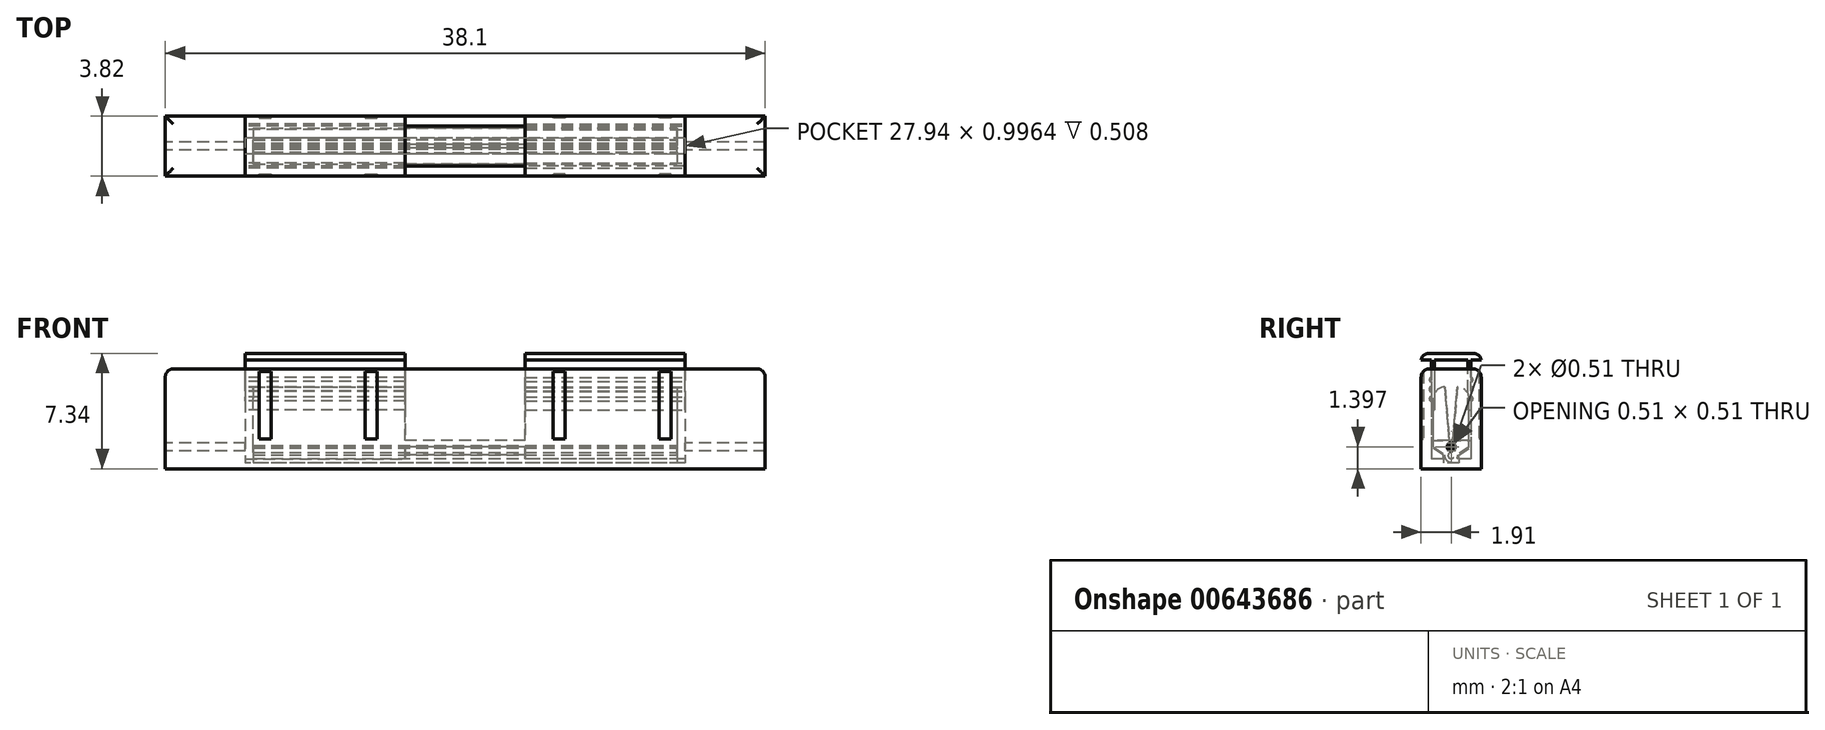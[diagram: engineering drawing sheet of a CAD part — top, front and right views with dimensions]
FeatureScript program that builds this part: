
annotation { "Feature Type Name" : "Feature", "Feature Type Description" : "" }
export const myFeature = defineFeature(function(context is Context, id is Id, definition is map)
    precondition{}
    {
        {
            var Q0;
            Q0=qCreatedBy(makeId("Top.planeOp"),FACE);
            var sketch = newSketch(context, id + "F0", { "sketchPlane" : qUnion([Q0])});
            skLineSegment(sketch, "E0.bottom", {"start": v(19.05, -1.9) * mm, "end": v(-19.05, -1.9) * mm});
            skLineSegment(sketch, "E0.top", {"start": v(19.05, 1.9) * mm, "end": v(-19.05, 1.9) * mm});
            skLineSegment(sketch, "E0.left", {"start": v(19.05, -1.9) * mm, "end": v(19.05, 1.9) * mm});
            skLineSegment(sketch, "E0.right", {"start": v(-19.05, -1.9) * mm, "end": v(-19.05, 1.9) * mm});
            skPoint(sketch, "E0.middle", {"position": v(0, 0) * mm});
            skLineSegment(sketch, "E1", {"start": v(0, 6.77) * mm, "end": v(0, -8.48) * mm, "construction": true});
            skLineSegment(sketch, "E2.bottom", {"start": v(-13.97, 1.27) * mm, "end": v(-3.81, 1.27) * mm});
            skLineSegment(sketch, "E2.top", {"start": v(-13.97, -1.27) * mm, "end": v(-3.81, -1.27) * mm});
            skLineSegment(sketch, "E2.left", {"start": v(-13.97, 1.27) * mm, "end": v(-13.97, -1.27) * mm});
            skLineSegment(sketch, "E2.right", {"start": v(-3.81, 1.27) * mm, "end": v(-3.81, -1.27) * mm});
            skLineSegment(sketch, "E3.MirrorCS", {"start": v(3.81, 1.27) * mm, "end": v(3.81, -1.27) * mm});
            skLineSegment(sketch, "E4.MirrorCS", {"start": v(13.97, 1.27) * mm, "end": v(3.81, 1.27) * mm});
            skLineSegment(sketch, "E5.MirrorCS", {"start": v(13.97, -1.27) * mm, "end": v(3.81, -1.27) * mm});
            skLineSegment(sketch, "E6.MirrorCS", {"start": v(13.97, 1.27) * mm, "end": v(13.97, -1.27) * mm});
            skLineSegment(sketch, "E7", {"start": v(13.08, 1.9) * mm, "end": v(13.08, 1.78) * mm});
            skLineSegment(sketch, "E8", {"start": v(13.08, 1.78) * mm, "end": v(12.32, 1.78) * mm});
            skLineSegment(sketch, "E9", {"start": v(12.32, 1.78) * mm, "end": v(12.32, 1.9) * mm});
            skLineSegment(sketch, "E10", {"start": v(26.93, 0) * mm, "end": v(-31.8, 0) * mm, "construction": true});
            skPoint(sketch, "E10.startSnap0", {"position": v(19.05, 0) * mm});
            skLineSegment(sketch, "E11", {"start": v(6.35, 1.9) * mm, "end": v(6.35, 1.78) * mm});
            skLineSegment(sketch, "E12", {"start": v(6.35, 1.78) * mm, "end": v(5.59, 1.78) * mm});
            skLineSegment(sketch, "E13", {"start": v(5.59, 1.78) * mm, "end": v(5.59, 1.9) * mm});
            skLineSegment(sketch, "E14.MirrorCS", {"start": v(6.35, -1.9) * mm, "end": v(6.35, -1.78) * mm});
            skLineSegment(sketch, "E15.MirrorCS", {"start": v(6.35, -1.78) * mm, "end": v(5.59, -1.78) * mm});
            skLineSegment(sketch, "E16.MirrorCS", {"start": v(5.59, -1.78) * mm, "end": v(5.59, -1.9) * mm});
            skLineSegment(sketch, "E17.MirrorCS", {"start": v(12.32, -1.78) * mm, "end": v(12.32, -1.9) * mm});
            skLineSegment(sketch, "E18.MirrorCS", {"start": v(13.08, -1.78) * mm, "end": v(12.32, -1.78) * mm});
            skLineSegment(sketch, "E19.MirrorCS", {"start": v(13.08, -1.9) * mm, "end": v(13.08, -1.78) * mm});
            skLineSegment(sketch, "E20.MirrorCS", {"start": v(-6.35, 1.78) * mm, "end": v(-5.59, 1.78) * mm});
            skLineSegment(sketch, "E21.MirrorCS", {"start": v(-5.59, 1.78) * mm, "end": v(-5.59, 1.9) * mm});
            skLineSegment(sketch, "E22.MirrorCS", {"start": v(-6.35, 1.9) * mm, "end": v(-6.35, 1.78) * mm});
            skLineSegment(sketch, "E23.MirrorCS", {"start": v(-12.32, 1.78) * mm, "end": v(-12.32, 1.9) * mm});
            skLineSegment(sketch, "E24.MirrorCS", {"start": v(-13.08, 1.78) * mm, "end": v(-12.32, 1.78) * mm});
            skLineSegment(sketch, "E25.MirrorCS", {"start": v(-13.08, 1.9) * mm, "end": v(-13.08, 1.78) * mm});
            skLineSegment(sketch, "E26.MirrorCS", {"start": v(-6.35, -1.9) * mm, "end": v(-6.35, -1.78) * mm});
            skLineSegment(sketch, "E27.MirrorCS", {"start": v(-6.35, -1.78) * mm, "end": v(-5.59, -1.78) * mm});
            skLineSegment(sketch, "E28.MirrorCS", {"start": v(-5.59, -1.78) * mm, "end": v(-5.59, -1.9) * mm});
            skLineSegment(sketch, "E29.MirrorCS", {"start": v(-13.08, -1.9) * mm, "end": v(-13.08, -1.78) * mm});
            skLineSegment(sketch, "E30.MirrorCS", {"start": v(-13.08, -1.78) * mm, "end": v(-12.32, -1.78) * mm});
            skLineSegment(sketch, "E31.MirrorCS", {"start": v(-12.32, -1.78) * mm, "end": v(-12.32, -1.9) * mm});
            skSolve(sketch);
        }
        {
            var Q0;
            Q0=makeQuery(id+"F0.imprint","IMPRINT",FACE,{"disambiguationData":[TD([[makeQuery(id+"F0.imprint","IMPRINT",EDGE,{"derivedFrom":sQuery(id+"F0.wireOp",EDGE,"E0.top")}),1.0]])]});
            extrude(context, id + "F1", {"entities" : qUnion([Q0]), "depth" : 6.35 * mm, "offsetDistance" : 25.4 * mm});
        }
        {
            var Q0;
            Q0=makeQuery(id+"F0.imprint","IMPRINT",FACE,{"disambiguationData":[TD([[makeQuery(id+"F0.imprint","IMPRINT",EDGE,{"derivedFrom":sQuery(id+"F0.wireOp",EDGE,"E2.bottom")}),-1.0]])]});
            var Q1;
            Q1=makeQuery(id+"F0.imprint","IMPRINT",FACE,{"disambiguationData":[TD([[makeQuery(id+"F0.imprint","IMPRINT",EDGE,{"derivedFrom":sQuery(id+"F0.wireOp",EDGE,"E3.MirrorCS")}),1.0]])]});
            extrude(context, id + "F2", {"entities" : qUnion([Q0, Q1]), "operationType" : NewBodyOperationType.ADD, "depth" : 0.64 * mm, "offsetDistance" : 25.4 * mm});
        }
        {
            var Q0;
            Q0=makeQuery(id+"F1.opExtrude","SWEPT_FACE",FACE,{"disambiguationData":[OSD([sQuery(id+"F0.wireOp",EDGE,"E2.left")])]});
            var sketch = newSketch(context, id + "F3", { "sketchPlane" : qUnion([Q0])});
            skLineSegment(sketch, "E32.bottom", {"start": v(0.5, 0.38) * mm, "end": v(-0.5, 0.38) * mm});
            skLineSegment(sketch, "E32.top", {"start": v(1.27, 5.46) * mm, "end": v(-1.27, 5.46) * mm});
            skLineSegment(sketch, "E32.left", {"start": v(1.27, 1.4) * mm, "end": v(1.27, 5.46) * mm});
            skLineSegment(sketch, "E32.right", {"start": v(-1.27, 1.4) * mm, "end": v(-1.27, 5.46) * mm});
            skLineSegment(sketch, "E33", {"start": v(0, 0) * mm, "end": v(0, 8.58) * mm, "construction": true});
            skPoint(sketch, "E34", {"position": v(0, 0.99) * mm});
            skLineSegment(sketch, "E35", {"start": v(0.5, 0.89) * mm, "end": v(0.5, 0.38) * mm});
            skLineSegment(sketch, "E36.MirrorCS", {"start": v(-0.5, 0.89) * mm, "end": v(-0.5, 0.38) * mm});
            skPoint(sketch, "E37.orphan", {"position": v(-0.5, 0.38) * mm});
            skPoint(sketch, "E38.orphan", {"position": v(1.27, 0.38) * mm});
            skLineSegment(sketch, "E39", {"start": v(1.27, 1.4) * mm, "end": v(0.5, 0.89) * mm});
            skLineSegment(sketch, "E40.MirrorCS", {"start": v(-1.27, 1.4) * mm, "end": v(-0.5, 0.89) * mm});
            skSolve(sketch);
        }
        {
            var Q0;
            Q0 = qSketchRegion(id + "F3", true);
            var Q1;
            Q1=makeQuery(id+"F1.opExtrude","SWEPT_FACE",FACE,{"disambiguationData":[OSD([sQuery(id+"F0.wireOp",EDGE,"E6.MirrorCS")])]});
            extrude(context, id + "F4", {"entities" : qUnion([Q0]), "operationType" : NewBodyOperationType.REMOVE, "endBound" : BoundingType.UP_TO_SURFACE, "depth" : 10.4 * mm, "endBoundEntityFace" : qUnion([Q1]), "offsetDistance" : 25.4 * mm});
        }
        {
            var Q0;
            Q0=qCreatedBy(makeId("Right.planeOp"),FACE);
            var sketch = newSketch(context, id + "F5", { "sketchPlane" : qUnion([Q0])});
            skCircle(sketch, "E41", {"center": v(0, 1.4) * mm, "radius": 0.1 * mm});
            skLineSegment(sketch, "E42.bottom", {"start": v(1.02, 5.08) * mm, "end": v(-1.02, 5.08) * mm});
            skLineSegment(sketch, "E42.top", {"start": v(1.02, 0) * mm, "end": v(-1.02, 0) * mm});
            skLineSegment(sketch, "E42.left", {"start": v(1.02, 5.08) * mm, "end": v(1.02, 0) * mm});
            skLineSegment(sketch, "E42.right", {"start": v(-1.02, 5.08) * mm, "end": v(-1.02, 0) * mm});
            skLineSegment(sketch, "E43", {"start": v(0, -1.4) * mm, "end": v(0, 7.34) * mm, "construction": true});
            skSolve(sketch);
        }
        {
            var Q0;
            Q0=makeQuery(id+"F1.opExtrude","SWEPT_FACE",FACE,{"disambiguationData":[OSD([sQuery(id+"F0.wireOp",EDGE,"E0.right")])]});
            var sketch = newSketch(context, id + "F6", { "sketchPlane" : qUnion([Q0])});
            skCircle(sketch, "E44", {"center": v(0, 1.4) * mm, "radius": 0.25 * mm});
            skSolve(sketch);
        }
        {
            var Q0;
            Q0 = qSketchRegion(id + "F6", true);
            extrude(context, id + "F7", {"entities" : qUnion([Q0]), "operationType" : NewBodyOperationType.REMOVE, "endBound" : BoundingType.THROUGH_ALL, "oppositeDirection" : true, "depth" : 25.4 * mm, "offsetDistance" : 25.4 * mm});
        }
        {
            var Q0;
            Q0=makeQuery(id+"F1.opExtrude","CAP_EDGE",EDGE,{"disambiguationData":[OSD([sQuery(id+"F0.wireOp",EDGE,"E0.right")])],"isStart":false});
            var Q1;
            Q1=makeQuery(id+"F1.opExtrude","CAP_EDGE",EDGE,{"disambiguationData":[OSD([sQuery(id+"F0.wireOp",EDGE,"E0.top")])],"isStart":false});
            var Q2;
            Q2=makeQuery(id+"F1.opExtrude","CAP_EDGE",EDGE,{"disambiguationData":[OSD([sQuery(id+"F0.wireOp",EDGE,"E0.bottom")])],"isStart":false});
            var Q3;
            Q3=makeQuery(id+"F1.opExtrude","CAP_EDGE",EDGE,{"disambiguationData":[OSD([sQuery(id+"F0.wireOp",EDGE,"E0.left")])],"isStart":false});
            fillet(context, id + "F8", {"entities" : qUnion([Q0, Q1, Q2, Q3]), "radius" : 0.5 * mm, "tangentPropagation" : true, "allowEdgeOverflow" : false});
        }
        {
            var Q0;
            Q0=makeQuery(id+"F1.opExtrude","SWEPT_FACE",FACE,{"disambiguationData":[OSD([sQuery(id+"F0.wireOp",EDGE,"E2.right")])]});
            var sketch = newSketch(context, id + "F9", { "sketchPlane" : qUnion([Q0])});
            skLineSegment(sketch, "E45.bottom", {"start": v(-0.38, 5.2) * mm, "end": v(0.38, 5.2) * mm});
            skLineSegment(sketch, "E45.top", {"start": v(-1.14, 0.38) * mm, "end": v(1.14, 0.38) * mm});
            skLineSegment(sketch, "E45.left", {"start": v(-1.14, 4.45) * mm, "end": v(-1.14, 0.38) * mm});
            skLineSegment(sketch, "E45.right", {"start": v(1.14, 4.45) * mm, "end": v(1.14, 0.38) * mm});
            skPoint(sketch, "E46.visualSharp", {"position": v(1.14, 5.2) * mm});
            skArc(sketch, "E46.filletArc", {"start": v(1.14, 4.45) * mm, "mid": v(0.92, 4.98) * mm, "end": v(0.38, 5.2) * mm});
            skPoint(sketch, "E47.visualSharp", {"position": v(-1.14, 5.2) * mm});
            skArc(sketch, "E47.filletArc", {"start": v(-0.38, 5.2) * mm, "mid": v(-0.92, 4.98) * mm, "end": v(-1.14, 4.45) * mm});
            skPoint(sketch, "E48.trimOffspring.end.orphan", {"position": v(0, 0.38) * mm});
            skLineSegment(sketch, "E49", {"start": v(-0.38, 5.2) * mm, "end": v(-0.09, 1.48) * mm});
            skLineSegment(sketch, "E50.MirrorCS", {"start": v(0.38, 5.2) * mm, "end": v(0.09, 1.48) * mm});
            skArc(sketch, "E51", {"start": v(-0.05, 1.03) * mm, "mid": v(0, 0.65) * mm, "end": v(0.05, 1.03) * mm});
            skLineSegment(sketch, "E52.trimOffspring", {"start": v(-0.08, 1.34) * mm, "end": v(-0.05, 1.03) * mm});
            skLineSegment(sketch, "E53.trimOffspring", {"start": v(0.08, 1.34) * mm, "end": v(0.05, 1.03) * mm});
            skArc(sketch, "E54", {"start": v(-0.42, 0.9) * mm, "mid": v(0, 0.42) * mm, "end": v(0.42, 0.9) * mm});
            skLineSegment(sketch, "E55", {"start": v(-0.42, 0.9) * mm, "end": v(-1.14, 1.4) * mm});
            skLineSegment(sketch, "E56.MirrorCS", {"start": v(0.42, 0.9) * mm, "end": v(1.14, 1.4) * mm});
            skArc(sketch, "E57", {"start": v(-0.09, 1.48) * mm, "mid": v(-0.2, 1.4) * mm, "end": v(-0.08, 1.34) * mm});
            skPoint(sketch, "E57.first.point", {"position": v(-0.08, 1.34) * mm});
            skPoint(sketch, "E57.second.point", {"position": v(-0.09, 1.48) * mm});
            skPoint(sketch, "E57.third.point", {"position": v(-0.2, 1.42) * mm});
            skArc(sketch, "E58.MirrorCS", {"start": v(0.08, 1.34) * mm, "mid": v(0.13, 1.4) * mm, "end": v(0.09, 1.48) * mm});
            skPoint(sketch, "E59.MirrorC.end.orphan", {"position": v(0.09, 1.48) * mm});
            skPoint(sketch, "E59.MirrorC.start.orphan", {"position": v(0.08, 1.34) * mm});
            skLineSegment(sketch, "E60.trimOffspring", {"start": v(0.08, 1.34) * mm, "end": v(0.08, 1.34) * mm});
            skLineSegment(sketch, "E61.trimOffspring", {"start": v(-0.08, 1.34) * mm, "end": v(-0.08, 1.34) * mm});
            skSolve(sketch);
        }
        {
            var Q0;
            {var subQ3=sQuery(id+"F9.wireOp",EDGE,"E46.filletArc");Q0=makeQuery(id+"F9.imprint","IMPRINT",FACE,{"disambiguationData":[TD([[makeQuery(id+"F9.imprint","IMPRINT",EDGE,{"derivedFrom":subQ3}),1.0]])]});}
            var Q1;
            Q1=makeQuery(id+"F4.boolean.opBoolean","MERGE",FACE,{"derivedFrom":[makeQuery(id+"F1.opExtrude","SWEPT_FACE",FACE,{"disambiguationData":[OSD([sQuery(id+"F0.wireOp",EDGE,"E2.left")])]}),makeQuery(id+"F4.opExtrude","CAP_FACE",FACE,{"disambiguationData":[OSD([sQuery(id+"F3.wireOp",EDGE,"E32.bottom"),sQuery(id+"F3.wireOp",EDGE,"E32.top"),sQuery(id+"F3.wireOp",EDGE,"E32.left"),sQuery(id+"F3.wireOp",EDGE,"E32.right"),sQuery(id+"F3.wireOp",EDGE,"E35"),sQuery(id+"F3.wireOp",EDGE,"E36.MirrorCS"),sQuery(id+"F3.wireOp",EDGE,"E39"),sQuery(id+"F3.wireOp",EDGE,"E40.MirrorCS")])],"isStart":true})]});
            extrude(context, id + "F10", {"entities" : qUnion([Q0]), "endBound" : BoundingType.UP_TO_SURFACE, "depth" : 7.62 * mm, "endBoundEntityFace" : qUnion([Q1]), "hasOffset" : true, "offsetDistance" : 0.5 * mm});
        }
        {
            var Q0;
            Q0=makeQuery(id+"F10.opExtrude","CAP_FACE",FACE,{"disambiguationData":[OSD([sQuery(id+"F9.wireOp",EDGE,"E45.left"),sQuery(id+"F9.wireOp",EDGE,"E45.right"),sQuery(id+"F9.wireOp",EDGE,"E46.filletArc"),sQuery(id+"F9.wireOp",EDGE,"E47.filletArc"),sQuery(id+"F9.wireOp",EDGE,"E50.MirrorCS"),sQuery(id+"F9.wireOp",EDGE,"E51"),sQuery(id+"F9.wireOp",EDGE,"E52.trimOffspring"),sQuery(id+"F9.wireOp",EDGE,"E53.trimOffspring"),sQuery(id+"F9.wireOp",EDGE,"E54"),sQuery(id+"F9.wireOp",EDGE,"E55"),sQuery(id+"F9.wireOp",EDGE,"E56.MirrorCS"),sQuery(id+"F9.wireOp",EDGE,"E57"),sQuery(id+"F9.wireOp",EDGE,"E49"),sQuery(id+"F9.wireOp",EDGE,"E58.MirrorCS"),sQuery(id+"F9.wireOp",EDGE,"E60.trimOffspring"),sQuery(id+"F9.wireOp",EDGE,"E61.trimOffspring")])],"isStart":true});
            var Q1;
            {var subQ0=sQuery(id+"F0.wireOp",EDGE,"E6.MirrorCS");Q1=makeQuery(id+"F4.boolean.opBoolean","MERGE",FACE,{"derivedFrom":[makeQuery(id+"F1.opExtrude","SWEPT_FACE",FACE,{"disambiguationData":[OSD([subQ0])]}),makeQuery(id+"F4.opExtrude","CAP_FACE",FACE,{"disambiguationData":[OSD([subQ0])],"isStart":false})]});}
            extrude(context, id + "F11", {"entities" : qUnion([Q0]), "operationType" : NewBodyOperationType.ADD, "endBound" : BoundingType.UP_TO_SURFACE, "depth" : 25.4 * mm, "endBoundEntityFace" : qUnion([Q1]), "hasOffset" : true, "offsetDistance" : 0.5 * mm});
        }
        {
            var Q0;
            Q0=qCreatedBy(makeId("Right.planeOp"),FACE);
            var sketch = newSketch(context, id + "F12", { "sketchPlane" : qUnion([Q0])});
            skLineSegment(sketch, "E62.bottom", {"start": v(1.26, 5.32) * mm, "end": v(-1.26, 5.32) * mm});
            skLineSegment(sketch, "E62.top", {"start": v(1.26, 1.8) * mm, "end": v(-1.26, 1.8) * mm});
            skLineSegment(sketch, "E62.left", {"start": v(1.26, 5.32) * mm, "end": v(1.26, 1.8) * mm});
            skLineSegment(sketch, "E62.right", {"start": v(-1.26, 5.32) * mm, "end": v(-1.26, 1.8) * mm});
            skSolve(sketch);
        }
        {
            var Q0;
            Q0 = qSketchRegion(id + "F12", true);
            extrude(context, id + "F13", {"entities" : qUnion([Q0]), "operationType" : NewBodyOperationType.REMOVE, "endBound" : BoundingType.SYMMETRIC, "oppositeDirection" : true, "depth" : 7.62 * mm, "offsetDistance" : 25.4 * mm});
        }
        {
            var Q0;
            Q0=makeQuery(id+"F4.boolean.opBoolean","COPY",FACE,{"derivedFrom":makeQuery(id+"F4.opExtrude","SWEPT_FACE",FACE,{"disambiguationData":[OSD([sQuery(id+"F3.wireOp",EDGE,"E32.top")])]})});
            extrude(context, id + "F14", {"entities" : qUnion([Q0]), "operationType" : NewBodyOperationType.ADD, "depth" : 3.3 * mm, "offsetDistance" : 25.4 * mm});
        }
        {
            var Q0;
            Q0=makeQuery(id+"F4.boolean.opBoolean","MERGE",FACE,{"derivedFrom":[makeQuery(id+"F1.opExtrude","SWEPT_FACE",FACE,{"disambiguationData":[OSD([sQuery(id+"F0.wireOp",EDGE,"E2.left")])]}),makeQuery(id+"F4.opExtrude","CAP_FACE",FACE,{"disambiguationData":[OSD([sQuery(id+"F3.wireOp",EDGE,"E32.bottom"),sQuery(id+"F3.wireOp",EDGE,"E32.top"),sQuery(id+"F3.wireOp",EDGE,"E32.left"),sQuery(id+"F3.wireOp",EDGE,"E32.right"),sQuery(id+"F3.wireOp",EDGE,"E35"),sQuery(id+"F3.wireOp",EDGE,"E36.MirrorCS"),sQuery(id+"F3.wireOp",EDGE,"E39"),sQuery(id+"F3.wireOp",EDGE,"E40.MirrorCS")])],"isStart":true})]});
            var sketch = newSketch(context, id + "F15", { "sketchPlane" : qUnion([Q0])});
            skLineSegment(sketch, "E63.left", {"start": v(1.27, 4.32) * mm, "end": v(1.27, 4.57) * mm});
            skLineSegment(sketch, "E63.right", {"start": v(-1.27, 4.32) * mm, "end": v(-1.27, 4.57) * mm});
            skArc(sketch, "E64", {"start": v(-1.27, 5.2) * mm, "mid": v(-1.4, 5.08) * mm, "end": v(-1.27, 4.95) * mm});
            skArc(sketch, "E65", {"start": v(-1.27, 4.57) * mm, "mid": v(-1.4, 4.44) * mm, "end": v(-1.27, 4.32) * mm});
            skArc(sketch, "E66.MirrorC", {"start": v(1.27, 5.2) * mm, "mid": v(1.4, 5.08) * mm, "end": v(1.27, 4.95) * mm});
            skArc(sketch, "E67.MirrorC", {"start": v(1.27, 4.57) * mm, "mid": v(1.4, 4.45) * mm, "end": v(1.27, 4.32) * mm});
            skLineSegment(sketch, "E68.trimOffspring", {"start": v(-1.27, 4.95) * mm, "end": v(-1.27, 5.2) * mm});
            skLineSegment(sketch, "E69.trimOffspring", {"start": v(1.27, 4.95) * mm, "end": v(1.27, 5.2) * mm});
            skSolve(sketch);
        }
        {
            var Q0;
            Q0 = qSketchRegion(id + "F15", true);
            var Q1;
            {var subQ0=sQuery(id+"F3.wireOp",EDGE,"E32.top");var subQ1=sQuery(id+"F0.wireOp",EDGE,"E2.right");Q1=makeQuery(id+"F14.boolean.opBoolean","MERGE",FACE,{"derivedFrom":[makeQuery(id+"F4.boolean.opBoolean","SPLIT",FACE,{"disambiguationData":[TD([makeQuery(id+"F4.opExtrude","SWEPT_FACE",FACE,{"disambiguationData":[OSD([subQ0])]})])],"derivedFrom":makeQuery(id+"F1.opExtrude","SWEPT_FACE",FACE,{"disambiguationData":[OSD([subQ1])]})}),makeQuery(id+"F14.opExtrude","SWEPT_FACE",FACE,{"disambiguationData":[OSD([subQ1,subQ0])]})]});}
            extrude(context, id + "F16", {"entities" : qUnion([Q0]), "operationType" : NewBodyOperationType.REMOVE, "endBound" : BoundingType.UP_TO_SURFACE, "depth" : 25.4 * mm, "endBoundEntityFace" : qUnion([Q1]), "offsetDistance" : 25.4 * mm});
        }
        {
            var Q0;
            {var subQ0=sQuery(id+"F0.wireOp",EDGE,"E6.MirrorCS");Q0=makeQuery(id+"F4.boolean.opBoolean","MERGE",FACE,{"derivedFrom":[makeQuery(id+"F1.opExtrude","SWEPT_FACE",FACE,{"disambiguationData":[OSD([subQ0])]}),makeQuery(id+"F4.opExtrude","CAP_FACE",FACE,{"disambiguationData":[OSD([subQ0])],"isStart":false})]});}
            var sketch = newSketch(context, id + "F17", { "sketchPlane" : qUnion([Q0])});
            skLineSegment(sketch, "E70.left", {"start": v(1.27, 4.32) * mm, "end": v(1.27, 4.57) * mm});
            skLineSegment(sketch, "E70.right", {"start": v(-1.27, 4.32) * mm, "end": v(-1.27, 4.57) * mm});
            skArc(sketch, "E71", {"start": v(-1.27, 5.2) * mm, "mid": v(-1.4, 5.08) * mm, "end": v(-1.27, 4.95) * mm});
            skArc(sketch, "E72", {"start": v(-1.27, 4.57) * mm, "mid": v(-1.4, 4.45) * mm, "end": v(-1.27, 4.32) * mm});
            skArc(sketch, "E73.MirrorC", {"start": v(1.27, 5.2) * mm, "mid": v(1.4, 5.08) * mm, "end": v(1.27, 4.95) * mm});
            skArc(sketch, "E74.MirrorC", {"start": v(1.27, 4.57) * mm, "mid": v(1.4, 4.45) * mm, "end": v(1.27, 4.32) * mm});
            skLineSegment(sketch, "E75.trimOffspring", {"start": v(-1.27, 4.95) * mm, "end": v(-1.27, 5.2) * mm});
            skLineSegment(sketch, "E76.trimOffspring", {"start": v(1.27, 4.95) * mm, "end": v(1.27, 5.2) * mm});
            skSolve(sketch);
        }
        {
            var Q0;
            Q0 = qSketchRegion(id + "F17", true);
            var Q1;
            {var subQ0=sQuery(id+"F3.wireOp",EDGE,"E32.top");var subQ1=sQuery(id+"F0.wireOp",EDGE,"E3.MirrorCS");Q1=makeQuery(id+"F14.boolean.opBoolean","MERGE",FACE,{"derivedFrom":[makeQuery(id+"F4.boolean.opBoolean","SPLIT",FACE,{"disambiguationData":[TD([makeQuery(id+"F4.opExtrude","SWEPT_FACE",FACE,{"disambiguationData":[OSD([subQ0])]})])],"derivedFrom":makeQuery(id+"F1.opExtrude","SWEPT_FACE",FACE,{"disambiguationData":[OSD([subQ1])]})}),makeQuery(id+"F14.opExtrude","SWEPT_FACE",FACE,{"disambiguationData":[OSD([subQ1,subQ0])]})]});}
            extrude(context, id + "F18", {"entities" : qUnion([Q0]), "operationType" : NewBodyOperationType.REMOVE, "endBound" : BoundingType.UP_TO_SURFACE, "depth" : 25.4 * mm, "endBoundEntityFace" : qUnion([Q1]), "offsetDistance" : 25.4 * mm});
        }
        {
            var Q0;
            {var subQ0=sQuery(id+"F0.wireOp",EDGE,"E6.MirrorCS");Q0=makeQuery(id+"F18.boolean.opBoolean","MERGE",FACE,{"derivedFrom":[makeQuery(id+"F4.boolean.opBoolean","MERGE",FACE,{"derivedFrom":[makeQuery(id+"F1.opExtrude","SWEPT_FACE",FACE,{"disambiguationData":[OSD([subQ0])]}),makeQuery(id+"F4.opExtrude","CAP_FACE",FACE,{"disambiguationData":[OSD([subQ0])],"isStart":false})]}),makeQuery(id+"F18.opExtrude","CAP_FACE",FACE,{"disambiguationData":[OSD([sQuery(id+"F17.wireOp",EDGE,"E70.left"),sQuery(id+"F17.wireOp",EDGE,"E74.MirrorC")])],"isStart":true}),makeQuery(id+"F18.opExtrude","CAP_FACE",FACE,{"disambiguationData":[OSD([sQuery(id+"F17.wireOp",EDGE,"E70.right"),sQuery(id+"F17.wireOp",EDGE,"E72")])],"isStart":true}),makeQuery(id+"F18.opExtrude","CAP_FACE",FACE,{"disambiguationData":[OSD([sQuery(id+"F17.wireOp",EDGE,"E71"),sQuery(id+"F17.wireOp",EDGE,"E75.trimOffspring")])],"isStart":true}),makeQuery(id+"F18.opExtrude","CAP_FACE",FACE,{"disambiguationData":[OSD([sQuery(id+"F17.wireOp",EDGE,"E73.MirrorC"),sQuery(id+"F17.wireOp",EDGE,"E76.trimOffspring")])],"isStart":true})]});}
            var sketch = newSketch(context, id + "F19", { "sketchPlane" : qUnion([Q0])});
            skLineSegment(sketch, "E77.bottom", {"start": v(-1.27, 3.74) * mm, "end": v(-1.07, 3.74) * mm});
            skLineSegment(sketch, "E77.top", {"start": v(-1.07, 6.92) * mm, "end": v(1.07, 6.92) * mm});
            skLineSegment(sketch, "E77.left", {"start": v(-1.27, 3.74) * mm, "end": v(-1.27, 4.9) * mm});
            skLineSegment(sketch, "E77.right", {"start": v(1.27, 3.74) * mm, "end": v(1.27, 4.9) * mm});
            skLineSegment(sketch, "E78.bottom", {"start": v(-1.9, 7.34) * mm, "end": v(1.9, 7.34) * mm});
            skLineSegment(sketch, "E78.top", {"start": v(-1.9, 6.92) * mm, "end": v(-1.27, 6.92) * mm});
            skLineSegment(sketch, "E78.left", {"start": v(-1.9, 7.34) * mm, "end": v(-1.9, 6.92) * mm});
            skLineSegment(sketch, "E78.right", {"start": v(1.9, 7.34) * mm, "end": v(1.9, 6.92) * mm});
            skLineSegment(sketch, "E79.0", {"start": v(-1.07, 3.94) * mm, "end": v(-1.07, 6.92) * mm});
            skLineSegment(sketch, "E79.2", {"start": v(1.07, 4.4) * mm, "end": v(1.07, 6.92) * mm});
            skLineSegment(sketch, "E80", {"start": v(-1.07, 3.94) * mm, "end": v(-1.07, 3.74) * mm});
            skLineSegment(sketch, "E81", {"start": v(1.07, 4.4) * mm, "end": v(1.07, 3.74) * mm});
            skLineSegment(sketch, "E82.trimOffspring", {"start": v(1.07, 3.74) * mm, "end": v(1.27, 3.74) * mm});
            skLineSegment(sketch, "E83.trimOffspring", {"start": v(1.27, 6.92) * mm, "end": v(1.9, 6.92) * mm});
            skArc(sketch, "E84", {"start": v(1.27, 5.54) * mm, "mid": v(1.4, 5.67) * mm, "end": v(1.27, 5.8) * mm});
            skPoint(sketch, "E84.centerSnap0", {"position": v(1.07, 5.67) * mm});
            skArc(sketch, "E85", {"start": v(1.27, 4.9) * mm, "mid": v(1.4, 5.03) * mm, "end": v(1.27, 5.16) * mm});
            skLineSegment(sketch, "E86", {"start": v(0, 6.92) * mm, "end": v(0, 3.1) * mm, "construction": true});
            skArc(sketch, "E87.MirrorCS", {"start": v(-1.27, 5.54) * mm, "mid": v(-1.4, 5.67) * mm, "end": v(-1.27, 5.8) * mm});
            skArc(sketch, "E88.MirrorCS", {"start": v(-1.27, 4.9) * mm, "mid": v(-1.4, 5.03) * mm, "end": v(-1.27, 5.16) * mm});
            skLineSegment(sketch, "E89.trimOffspring", {"start": v(-1.27, 5.8) * mm, "end": v(-1.27, 6.92) * mm});
            skLineSegment(sketch, "E90.trimOffspring", {"start": v(-1.27, 5.16) * mm, "end": v(-1.27, 5.54) * mm});
            skLineSegment(sketch, "E91.trimOffspring", {"start": v(1.27, 5.16) * mm, "end": v(1.27, 5.54) * mm});
            skLineSegment(sketch, "E92.trimOffspring", {"start": v(1.27, 5.8) * mm, "end": v(1.27, 6.92) * mm});
            skSolve(sketch);
        }
        {
            var Q0;
            Q0 = qSketchRegion(id + "F19", true);
            var Q1;
            {var subQ0=sQuery(id+"F3.wireOp",EDGE,"E32.top");var subQ1=sQuery(id+"F0.wireOp",EDGE,"E3.MirrorCS");Q1=makeQuery(id+"F18.boolean.opBoolean","MERGE",FACE,{"derivedFrom":[makeQuery(id+"F14.boolean.opBoolean","MERGE",FACE,{"derivedFrom":[makeQuery(id+"F4.boolean.opBoolean","SPLIT",FACE,{"disambiguationData":[TD([makeQuery(id+"F4.opExtrude","SWEPT_FACE",FACE,{"disambiguationData":[OSD([subQ0])]})])],"derivedFrom":makeQuery(id+"F1.opExtrude","SWEPT_FACE",FACE,{"disambiguationData":[OSD([subQ1])]})}),makeQuery(id+"F14.opExtrude","SWEPT_FACE",FACE,{"disambiguationData":[OSD([subQ1,subQ0])]})]}),makeQuery(id+"F18.opExtrude","CAP_FACE",FACE,{"disambiguationData":[OSD([sQuery(id+"F17.wireOp",EDGE,"E70.left"),sQuery(id+"F17.wireOp",EDGE,"E74.MirrorC")])],"isStart":false}),makeQuery(id+"F18.opExtrude","CAP_FACE",FACE,{"disambiguationData":[OSD([sQuery(id+"F17.wireOp",EDGE,"E70.right"),sQuery(id+"F17.wireOp",EDGE,"E72")])],"isStart":false}),makeQuery(id+"F18.opExtrude","CAP_FACE",FACE,{"disambiguationData":[OSD([sQuery(id+"F17.wireOp",EDGE,"E71"),sQuery(id+"F17.wireOp",EDGE,"E75.trimOffspring")])],"isStart":false}),makeQuery(id+"F18.opExtrude","CAP_FACE",FACE,{"disambiguationData":[OSD([sQuery(id+"F17.wireOp",EDGE,"E73.MirrorC"),sQuery(id+"F17.wireOp",EDGE,"E76.trimOffspring")])],"isStart":false})]});}
            extrude(context, id + "F20", {"entities" : qUnion([Q0]), "endBound" : BoundingType.UP_TO_SURFACE, "depth" : 25.4 * mm, "endBoundEntityFace" : qUnion([Q1]), "offsetDistance" : 25.4 * mm});
        }
        {
            var Q0;
            Q0=makeQuery(id+"F20.opExtrude","SWEPT_EDGE",EDGE,{"disambiguationData":[OSD([sQuery(id+"F19.wireOp",EDGE,"E78.bottom"),sQuery(id+"F19.wireOp",EDGE,"E78.left")])]});
            var Q1;
            Q1=makeQuery(id+"F20.opExtrude","SWEPT_EDGE",EDGE,{"disambiguationData":[OSD([sQuery(id+"F19.wireOp",EDGE,"E78.bottom"),sQuery(id+"F19.wireOp",EDGE,"E78.right")])]});
            fillet(context, id + "F21", {"entities" : qUnion([Q0, Q1]), "radius" : 0.5 * mm, "tangentPropagation" : true, "allowEdgeOverflow" : false});
        }
        {
            var Q0;
            Q0=makeQuery(id+"F3.imprint","IMPRINT",FACE,{"disambiguationData":[TD([[makeQuery(id+"F3.imprint","IMPRINT",EDGE,{"derivedFrom":sQuery(id+"F3.wireOp",EDGE,"E32.top")}),1.0]])]});
            var sketch = newSketch(context, id + "F22", { "sketchPlane" : qUnion([Q0])});
            skLineSegment(sketch, "E93.bottom", {"start": v(-1.27, 3.74) * mm, "end": v(-1.07, 3.74) * mm});
            skLineSegment(sketch, "E93.top", {"start": v(-1.07, 6.92) * mm, "end": v(1.07, 6.92) * mm});
            skLineSegment(sketch, "E93.left", {"start": v(-1.27, 3.74) * mm, "end": v(-1.27, 4.9) * mm});
            skLineSegment(sketch, "E93.right", {"start": v(1.27, 3.74) * mm, "end": v(1.27, 4.9) * mm});
            skLineSegment(sketch, "E94.bottom", {"start": v(-1.9, 7.34) * mm, "end": v(1.9, 7.34) * mm});
            skLineSegment(sketch, "E94.top", {"start": v(-1.9, 6.92) * mm, "end": v(-1.27, 6.92) * mm});
            skLineSegment(sketch, "E94.left", {"start": v(-1.9, 7.34) * mm, "end": v(-1.9, 6.92) * mm});
            skLineSegment(sketch, "E94.right", {"start": v(1.9, 7.34) * mm, "end": v(1.9, 6.92) * mm});
            skLineSegment(sketch, "E95.0", {"start": v(-1.07, 3.94) * mm, "end": v(-1.07, 6.92) * mm});
            skLineSegment(sketch, "E95.2", {"start": v(1.07, 4.4) * mm, "end": v(1.07, 6.92) * mm});
            skLineSegment(sketch, "E96", {"start": v(-1.07, 3.94) * mm, "end": v(-1.07, 3.74) * mm});
            skLineSegment(sketch, "E97", {"start": v(1.07, 4.4) * mm, "end": v(1.07, 3.74) * mm});
            skLineSegment(sketch, "E98.trimOffspring", {"start": v(1.07, 3.74) * mm, "end": v(1.27, 3.74) * mm});
            skLineSegment(sketch, "E99.trimOffspring", {"start": v(1.27, 6.92) * mm, "end": v(1.9, 6.92) * mm});
            skArc(sketch, "E100", {"start": v(1.27, 5.54) * mm, "mid": v(1.4, 5.67) * mm, "end": v(1.27, 5.8) * mm});
            skPoint(sketch, "E100.centerSnap0", {"position": v(1.07, 5.67) * mm});
            skArc(sketch, "E101", {"start": v(1.27, 4.9) * mm, "mid": v(1.4, 5.03) * mm, "end": v(1.27, 5.16) * mm});
            skLineSegment(sketch, "E102", {"start": v(0, 6.92) * mm, "end": v(0, 3.1) * mm, "construction": true});
            skArc(sketch, "E103.MirrorCS", {"start": v(-1.27, 5.54) * mm, "mid": v(-1.4, 5.67) * mm, "end": v(-1.27, 5.8) * mm});
            skArc(sketch, "E104.MirrorCS", {"start": v(-1.27, 4.9) * mm, "mid": v(-1.4, 5.03) * mm, "end": v(-1.27, 5.16) * mm});
            skLineSegment(sketch, "E105.trimOffspring", {"start": v(-1.27, 5.8) * mm, "end": v(-1.27, 6.92) * mm});
            skLineSegment(sketch, "E106.trimOffspring", {"start": v(-1.27, 5.16) * mm, "end": v(-1.27, 5.54) * mm});
            skLineSegment(sketch, "E107.trimOffspring", {"start": v(1.27, 5.16) * mm, "end": v(1.27, 5.54) * mm});
            skLineSegment(sketch, "E108.trimOffspring", {"start": v(1.27, 5.8) * mm, "end": v(1.27, 6.92) * mm});
            skSolve(sketch);
        }
        {
            var Q0;
            Q0 = qSketchRegion(id + "F22", true);
            var Q1;
            {var subQ0=sQuery(id+"F3.wireOp",EDGE,"E32.top");var subQ1=sQuery(id+"F0.wireOp",EDGE,"E2.right");Q1=makeQuery(id+"F16.boolean.opBoolean","MERGE",FACE,{"derivedFrom":[makeQuery(id+"F14.boolean.opBoolean","MERGE",FACE,{"derivedFrom":[makeQuery(id+"F4.boolean.opBoolean","SPLIT",FACE,{"disambiguationData":[TD([makeQuery(id+"F4.opExtrude","SWEPT_FACE",FACE,{"disambiguationData":[OSD([subQ0])]})])],"derivedFrom":makeQuery(id+"F1.opExtrude","SWEPT_FACE",FACE,{"disambiguationData":[OSD([subQ1])]})}),makeQuery(id+"F14.opExtrude","SWEPT_FACE",FACE,{"disambiguationData":[OSD([subQ1,subQ0])]})]}),makeQuery(id+"F16.opExtrude","CAP_FACE",FACE,{"disambiguationData":[OSD([sQuery(id+"F15.wireOp",EDGE,"E63.left"),sQuery(id+"F15.wireOp",EDGE,"E67.MirrorC")])],"isStart":false}),makeQuery(id+"F16.opExtrude","CAP_FACE",FACE,{"disambiguationData":[OSD([sQuery(id+"F15.wireOp",EDGE,"E63.right"),sQuery(id+"F15.wireOp",EDGE,"E65")])],"isStart":false}),makeQuery(id+"F16.opExtrude","CAP_FACE",FACE,{"disambiguationData":[OSD([sQuery(id+"F15.wireOp",EDGE,"E64"),sQuery(id+"F15.wireOp",EDGE,"E68.trimOffspring")])],"isStart":false}),makeQuery(id+"F16.opExtrude","CAP_FACE",FACE,{"disambiguationData":[OSD([sQuery(id+"F15.wireOp",EDGE,"E66.MirrorC"),sQuery(id+"F15.wireOp",EDGE,"E69.trimOffspring")])],"isStart":false})]});}
            extrude(context, id + "F23", {"entities" : qUnion([Q0]), "endBound" : BoundingType.UP_TO_SURFACE, "depth" : 25.4 * mm, "endBoundEntityFace" : qUnion([Q1]), "offsetDistance" : 25.4 * mm});
        }
        {
            var Q0;
            Q0=makeQuery(id+"F23.opExtrude","SWEPT_EDGE",EDGE,{"disambiguationData":[OSD([sQuery(id+"F22.wireOp",EDGE,"E94.bottom"),sQuery(id+"F22.wireOp",EDGE,"E94.left")])]});
            var Q1;
            Q1=makeQuery(id+"F23.opExtrude","SWEPT_EDGE",EDGE,{"disambiguationData":[OSD([sQuery(id+"F22.wireOp",EDGE,"E94.bottom"),sQuery(id+"F22.wireOp",EDGE,"E94.right")])]});
            fillet(context, id + "F24", {"entities" : qUnion([Q0, Q1]), "radius" : 0.5 * mm, "tangentPropagation" : true, "allowEdgeOverflow" : false});
        }
        {
            var Q0;
            Q0=makeQuery(id+"F1.opExtrude","CAP_FACE",FACE,{"disambiguationData":[OSD([sQuery(id+"F0.wireOp",EDGE,"E0.bottom"),sQuery(id+"F0.wireOp",EDGE,"E0.top"),sQuery(id+"F0.wireOp",EDGE,"E0.left"),sQuery(id+"F0.wireOp",EDGE,"E0.right"),sQuery(id+"F0.wireOp",EDGE,"E2.bottom"),sQuery(id+"F0.wireOp",EDGE,"E2.top"),sQuery(id+"F0.wireOp",EDGE,"E2.left"),sQuery(id+"F0.wireOp",EDGE,"E2.right"),sQuery(id+"F0.wireOp",EDGE,"E3.MirrorCS"),sQuery(id+"F0.wireOp",EDGE,"E4.MirrorCS"),sQuery(id+"F0.wireOp",EDGE,"E5.MirrorCS"),sQuery(id+"F0.wireOp",EDGE,"E6.MirrorCS")])],"isStart":false});
            var sketch = newSketch(context, id + "F25", { "sketchPlane" : qUnion([Q0])});
            skLineSegment(sketch, "E109.bottom", {"start": v(-3.81, 1.27) * mm, "end": v(3.81, 1.27) * mm});
            skLineSegment(sketch, "E109.top", {"start": v(-3.81, -1.27) * mm, "end": v(3.81, -1.27) * mm});
            skLineSegment(sketch, "E109.left", {"start": v(-3.81, 1.27) * mm, "end": v(-3.81, -1.27) * mm});
            skLineSegment(sketch, "E109.right", {"start": v(3.81, 1.27) * mm, "end": v(3.81, -1.27) * mm});
            skSolve(sketch);
        }
        {
            var Q0;
            Q0=makeQuery(id+"F25.imprint","IMPRINT",FACE,{"disambiguationData":[TD([[makeQuery(id+"F25.imprint","IMPRINT",EDGE,{"derivedFrom":sQuery(id+"F25.wireOp",EDGE,"E109.bottom")}),-1.0]])]});
            var Q1;
            {var subQ0=sQuery(id+"F9.wireOp",EDGE,"E45.left");var subQ4=sQuery(id+"F12.wireOp",EDGE,"E62.top");Q1=makeQuery(id+"F13.boolean.opBoolean","COPY",FACE,{"disambiguationData":[TD([makeQuery(id+"F10.opExtrude","SWEPT_FACE",FACE,{"disambiguationData":[OSD([subQ0])]})])],"derivedFrom":makeQuery(id+"F13.opExtrude","SWEPT_FACE",FACE,{"disambiguationData":[OSD([subQ4])]})});}
            extrude(context, id + "F26", {"entities" : qUnion([Q0]), "operationType" : NewBodyOperationType.REMOVE, "endBound" : BoundingType.UP_TO_SURFACE, "oppositeDirection" : true, "depth" : 25.4 * mm, "endBoundEntityFace" : qUnion([Q1]), "offsetDistance" : 25.4 * mm});
        }
        {
            var Q0;
            {var subQ0=sQuery(id+"F9.wireOp",EDGE,"E45.left");var subQ4=sQuery(id+"F12.wireOp",EDGE,"E62.top");Q0=makeQuery(id+"F13.boolean.opBoolean","COPY",FACE,{"disambiguationData":[TD([makeQuery(id+"F10.opExtrude","SWEPT_FACE",FACE,{"disambiguationData":[OSD([subQ0])]})])],"derivedFrom":makeQuery(id+"F13.opExtrude","SWEPT_FACE",FACE,{"disambiguationData":[OSD([subQ4])]})});}
            var sketch = newSketch(context, id + "F27", { "sketchPlane" : qUnion([Q0])});
            skLineSegment(sketch, "E110.bottom", {"start": v(3.81, -1.27) * mm, "end": v(-3.81, -1.27) * mm});
            skLineSegment(sketch, "E110.top", {"start": v(3.81, 1.27) * mm, "end": v(-3.81, 1.27) * mm});
            skLineSegment(sketch, "E110.left", {"start": v(3.81, -1.27) * mm, "end": v(3.81, 1.27) * mm});
            skLineSegment(sketch, "E110.right", {"start": v(-3.81, -1.27) * mm, "end": v(-3.81, 1.27) * mm});
            skPoint(sketch, "E110.middle", {"position": v(0, 0) * mm});
            skSolve(sketch);
        }
        {
            var Q0;
            Q0 = qSketchRegion(id + "F27", true);
            var Q1;
            Q1=makeQuery(id+"F1.opExtrude","CAP_FACE",FACE,{"disambiguationData":[OSD([sQuery(id+"F0.wireOp",EDGE,"E0.bottom"),sQuery(id+"F0.wireOp",EDGE,"E0.top"),sQuery(id+"F0.wireOp",EDGE,"E0.left"),sQuery(id+"F0.wireOp",EDGE,"E0.right"),sQuery(id+"F0.wireOp",EDGE,"E2.bottom"),sQuery(id+"F0.wireOp",EDGE,"E2.top"),sQuery(id+"F0.wireOp",EDGE,"E2.left"),sQuery(id+"F0.wireOp",EDGE,"E2.right"),sQuery(id+"F0.wireOp",EDGE,"E3.MirrorCS"),sQuery(id+"F0.wireOp",EDGE,"E4.MirrorCS"),sQuery(id+"F0.wireOp",EDGE,"E5.MirrorCS"),sQuery(id+"F0.wireOp",EDGE,"E6.MirrorCS")])],"isStart":false});
            var Q2;
            {var subQ1=sQuery(id+"F9.wireOp",EDGE,"E45.right");var subQ4=sQuery(id+"F12.wireOp",EDGE,"E62.top");Q2=makeQuery(id+"F13.boolean.opBoolean","COPY",FACE,{"disambiguationData":[TD([makeQuery(id+"F10.opExtrude","SWEPT_FACE",FACE,{"disambiguationData":[OSD([subQ1])]})])],"derivedFrom":makeQuery(id+"F13.opExtrude","SWEPT_FACE",FACE,{"disambiguationData":[OSD([subQ4])]})});}
            extrude(context, id + "F28", {"entities" : qUnion([Q0]), "endBound" : BoundingType.UP_TO_SURFACE, "depth" : 25.4 * mm, "endBoundEntityFace" : qUnion([Q1]), "offsetDistance" : 2.54 * mm});
        }
        {
            var Q0;
            {var subQ0=sQuery(id+"F0.wireOp",EDGE,"E29.MirrorCS");Q0=makeQuery(id+"F0.imprint","IMPRINT",FACE,{"disambiguationData":[TD([[makeQuery(id+"F0.imprint","IMPRINT",EDGE,{"derivedFrom":subQ0}),-1.0]])]});}
            var Q1;
            {var subQ0=sQuery(id+"F0.wireOp",EDGE,"E26.MirrorCS");Q1=makeQuery(id+"F0.imprint","IMPRINT",FACE,{"disambiguationData":[TD([[makeQuery(id+"F0.imprint","IMPRINT",EDGE,{"derivedFrom":subQ0}),-1.0]])]});}
            var Q2;
            Q2=makeQuery(id+"F0.imprint","IMPRINT",FACE,{"disambiguationData":[TD([[makeQuery(id+"F0.imprint","IMPRINT",EDGE,{"derivedFrom":sQuery(id+"F0.wireOp",EDGE,"E20.MirrorCS")}),1.0]])]});
            var Q3;
            {var subQ0=sQuery(id+"F0.wireOp",EDGE,"E23.MirrorCS");Q3=makeQuery(id+"F0.imprint","IMPRINT",FACE,{"disambiguationData":[TD([[makeQuery(id+"F0.imprint","IMPRINT",EDGE,{"derivedFrom":subQ0}),1.0]])]});}
            var Q4;
            {var subQ0=sQuery(id+"F0.wireOp",EDGE,"E14.MirrorCS");Q4=makeQuery(id+"F0.imprint","IMPRINT",FACE,{"disambiguationData":[TD([[makeQuery(id+"F0.imprint","IMPRINT",EDGE,{"derivedFrom":subQ0}),1.0]])]});}
            var Q5;
            {var subQ0=sQuery(id+"F0.wireOp",EDGE,"E17.MirrorCS");Q5=makeQuery(id+"F0.imprint","IMPRINT",FACE,{"disambiguationData":[TD([[makeQuery(id+"F0.imprint","IMPRINT",EDGE,{"derivedFrom":subQ0}),1.0]])]});}
            var Q6;
            {var subQ0=sQuery(id+"F0.wireOp",EDGE,"E7");Q6=makeQuery(id+"F0.imprint","IMPRINT",FACE,{"disambiguationData":[TD([[makeQuery(id+"F0.imprint","IMPRINT",EDGE,{"derivedFrom":subQ0}),-1.0]])]});}
            var Q7;
            {var subQ0=sQuery(id+"F0.wireOp",EDGE,"E11");Q7=makeQuery(id+"F0.imprint","IMPRINT",FACE,{"disambiguationData":[TD([[makeQuery(id+"F0.imprint","IMPRINT",EDGE,{"derivedFrom":subQ0}),-1.0]])]});}
            extrude(context, id + "F29", {"entities" : qUnion([Q0, Q1, Q2, Q3, Q4, Q5, Q6, Q7]), "operationType" : NewBodyOperationType.ADD, "depth" : 1.9 * mm, "offsetDistance" : 25.4 * mm});
        }
    });
